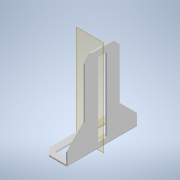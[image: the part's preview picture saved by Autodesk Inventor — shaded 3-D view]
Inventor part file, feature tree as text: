
AUTODESK INVENTOR PART (.ipt)
format: ipt  version: 2020 (Build 240168000, 168)  size: 144,384 bytes
history: native  units: in
note: dims shown in document units (in); Inventor stores cm internally (conversion verified against a paired STEP export)
features: other x2, plane x1, imported_body x1
ambient origin geometry x8: Origin, YZ Plane, XZ Plane, XY Plane, X Axis, Y Axis, Z Axis, Center Point
bodies: Body1 (feature_tree)
feature tree (4):
  other  "Angle Gusset"
  parser-record x1  (decoder bookkeeping rows leaked as tree rows — omitted from the tree; the rows remain in map.json)
  plane  "Work Plane1"
  imported_body  "Base1"
